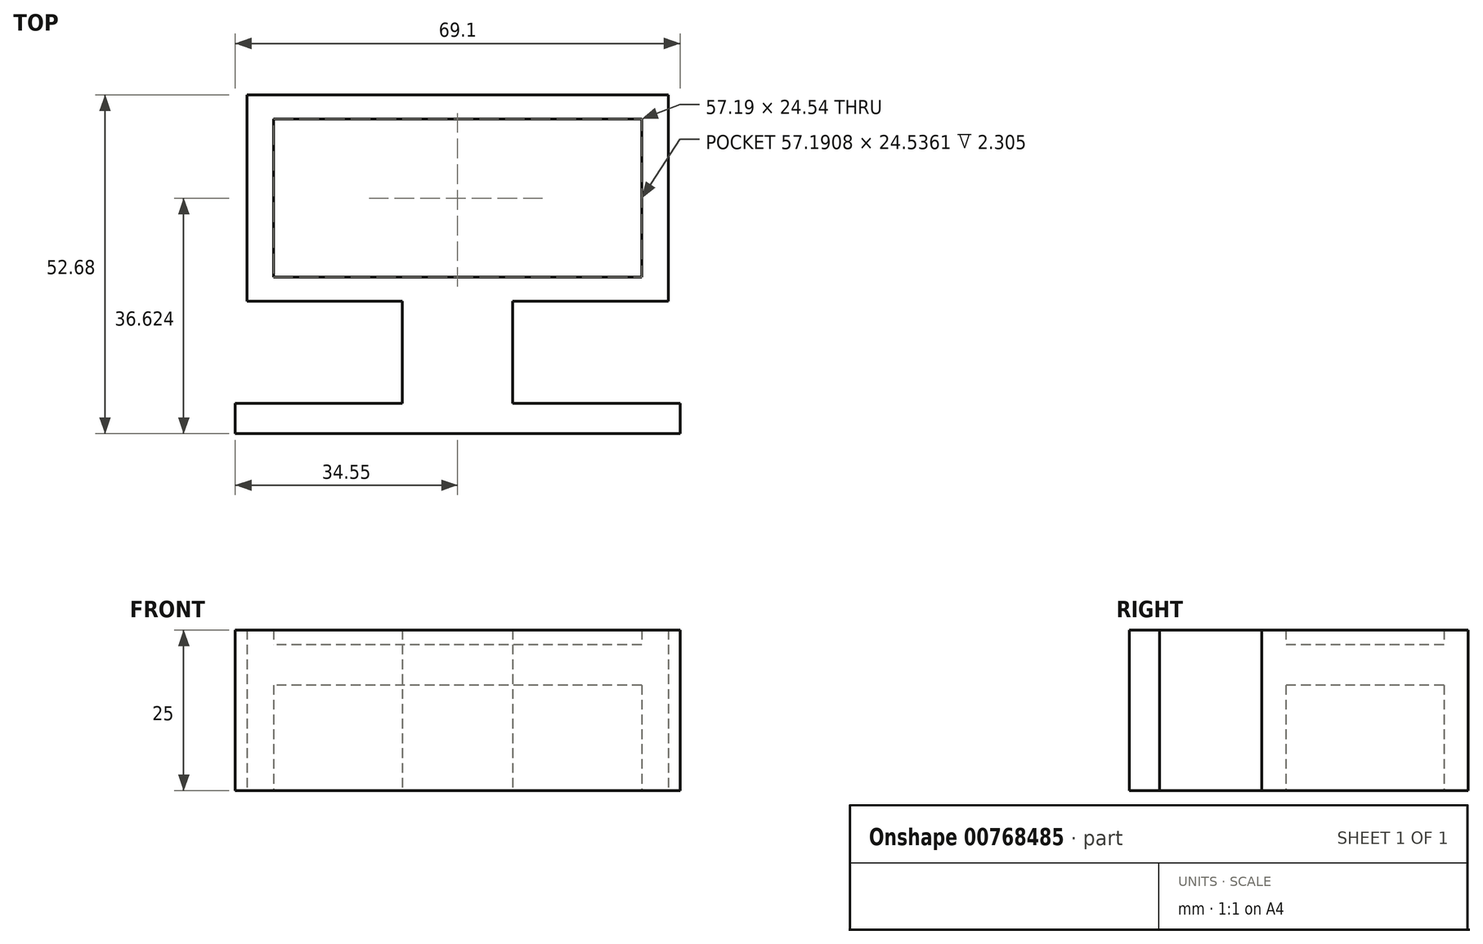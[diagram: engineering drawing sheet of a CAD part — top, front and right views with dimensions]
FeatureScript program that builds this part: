
annotation { "Feature Type Name" : "Feature", "Feature Type Description" : "" }
export const myFeature = defineFeature(function(context is Context, id is Id, definition is map)
    precondition{}
    {
        {
            var Q0;
            Q0=qCreatedBy(makeId("Top.planeOp"),FACE);
            var sketch = newSketch(context, id + "F0", { "sketchPlane" : qUnion([Q0])});
            skLineSegment(sketch, "E0.bottom", {"start": v(32.74, 48.35) * mm, "end": v(-32.74, 48.35) * mm});
            skLineSegment(sketch, "E0.top", {"start": v(32.74, 16.24) * mm, "end": v(-32.74, 16.24) * mm});
            skLineSegment(sketch, "E0.left", {"start": v(32.74, 48.35) * mm, "end": v(32.74, 16.24) * mm});
            skLineSegment(sketch, "E0.right", {"start": v(-32.74, 48.35) * mm, "end": v(-32.74, 16.24) * mm});
            skPoint(sketch, "E0.middle", {"position": v(0, 32.3) * mm});
            skLineSegment(sketch, "E1.bottom", {"start": v(28.6, 44.56) * mm, "end": v(-28.6, 44.56) * mm});
            skLineSegment(sketch, "E1.top", {"start": v(28.6, 20.03) * mm, "end": v(-28.6, 20.03) * mm});
            skLineSegment(sketch, "E1.left", {"start": v(28.6, 44.56) * mm, "end": v(28.6, 20.03) * mm});
            skLineSegment(sketch, "E1.right", {"start": v(-28.6, 44.56) * mm, "end": v(-28.6, 20.03) * mm});
            skLineSegment(sketch, "E2.bottom", {"start": v(-8.57, 16.24) * mm, "end": v(8.57, 16.24) * mm});
            skLineSegment(sketch, "E2.top", {"start": v(-8.57, 0) * mm, "end": v(8.57, 0) * mm});
            skLineSegment(sketch, "E2.left", {"start": v(-8.57, 16.24) * mm, "end": v(-8.57, 0) * mm});
            skLineSegment(sketch, "E2.right", {"start": v(8.57, 16.24) * mm, "end": v(8.57, 0) * mm});
            skLineSegment(sketch, "E3.bottom", {"start": v(34.55, -4.33) * mm, "end": v(-34.55, -4.33) * mm});
            skLineSegment(sketch, "E3.top", {"start": v(34.55, 0.36) * mm, "end": v(-34.55, 0.36) * mm});
            skLineSegment(sketch, "E3.left", {"start": v(34.55, -4.33) * mm, "end": v(34.55, 0.36) * mm});
            skLineSegment(sketch, "E3.right", {"start": v(-34.55, -4.33) * mm, "end": v(-34.55, 0.36) * mm});
            skPoint(sketch, "E3.middle", {"position": v(0, -1.98) * mm});
            skSolve(sketch);
        }
        {
            var Q0;
            Q0 = qSketchRegion(id + "F0", true);
            extrude(context, id + "F1", {"entities" : qUnion([Q0]), "depth" : 25 * mm, "offsetDistance" : 25 * mm});
        }
        {
            var Q0;
            Q0=makeQuery(id+"F1.opExtrude","SWEPT_FACE",FACE,{"disambiguationData":[OSD([sQuery(id+"F0.wireOp",EDGE,"E1.top")])]});
            var sketch = newSketch(context, id + "F2", { "sketchPlane" : qUnion([Q0])});
            skLineSegment(sketch, "E4.bottom", {"start": v(-28.6, 16.43) * mm, "end": v(28.6, 16.43) * mm});
            skLineSegment(sketch, "E4.top", {"start": v(-28.6, 22.7) * mm, "end": v(28.6, 22.7) * mm});
            skLineSegment(sketch, "E4.left", {"start": v(-28.6, 16.43) * mm, "end": v(-28.6, 22.7) * mm});
            skLineSegment(sketch, "E4.right", {"start": v(28.6, 16.43) * mm, "end": v(28.6, 22.7) * mm});
            skPoint(sketch, "E4.middle", {"position": v(0, 19.56) * mm});
            skSolve(sketch);
        }
        {
            var Q0;
            Q0 = qSketchRegion(id + "F2", true);
            extrude(context, id + "F3", {"entities" : qUnion([Q0]), "operationType" : NewBodyOperationType.ADD, "depth" : 25.4 * mm, "offsetDistance" : 25 * mm});
        }
    });
